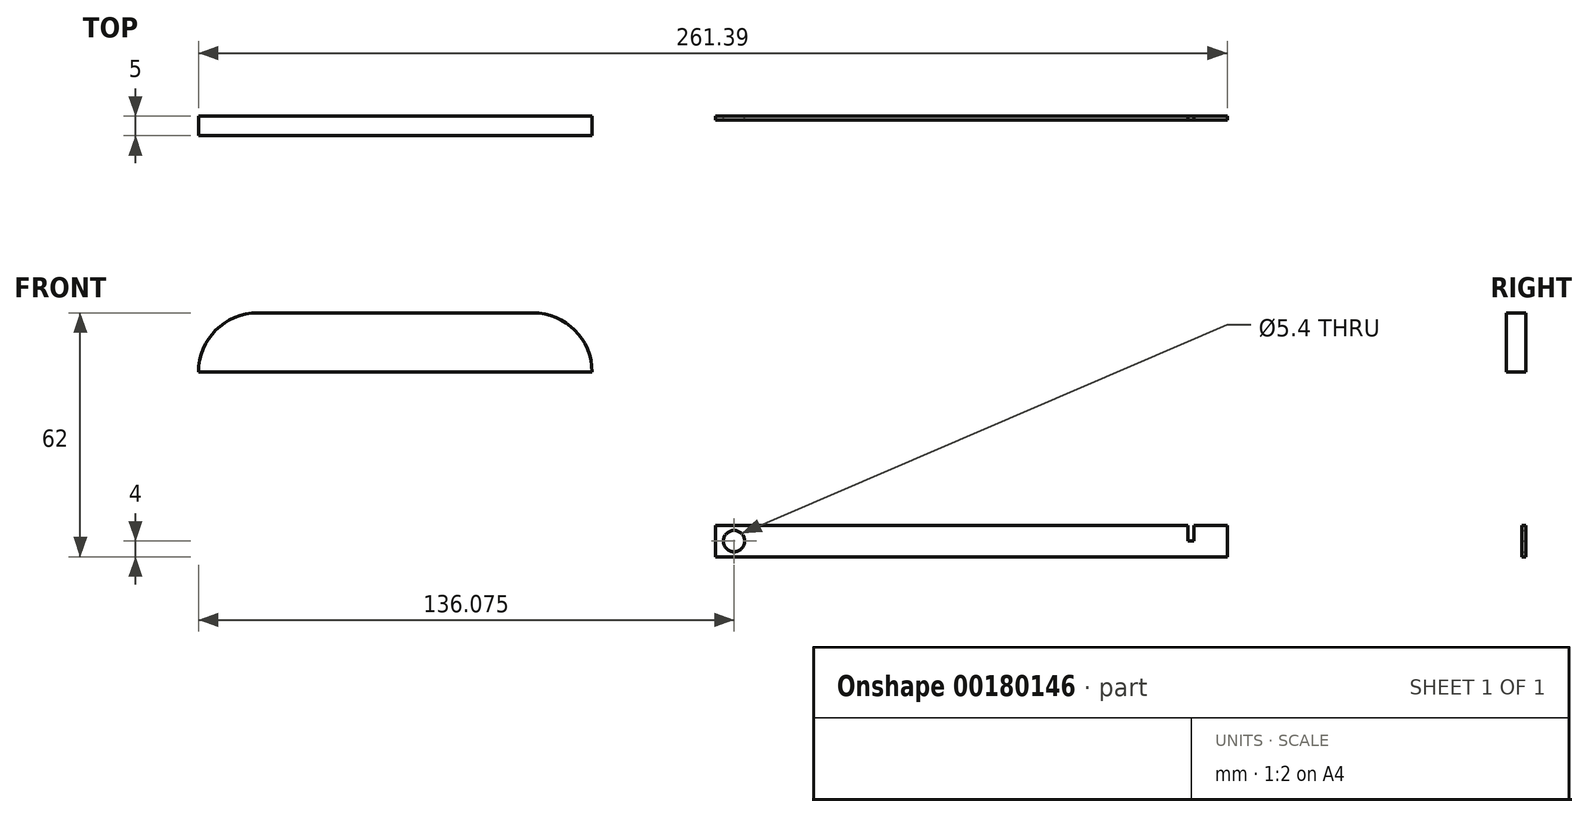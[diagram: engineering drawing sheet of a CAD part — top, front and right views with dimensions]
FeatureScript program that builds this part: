
annotation { "Feature Type Name" : "Feature", "Feature Type Description" : "" }
export const myFeature = defineFeature(function(context is Context, id is Id, definition is map)
    precondition{}
    {
        {
            var Q0;
            Q0=qCreatedBy(makeId("Front.planeOp"),FACE);
            var sketch = newSketch(context, id + "F0", { "sketchPlane" : qUnion([Q0])});
            skLineSegment(sketch, "E0", {"start": v(-91.47, 19.29) * mm, "end": v(8.53, 19.29) * mm});
            skLineSegment(sketch, "E1", {"start": v(8.53, 19.29) * mm, "end": v(8.53, 19.29) * mm});
            skLineSegment(sketch, "E2", {"start": v(-6.47, 34.29) * mm, "end": v(-76.47, 34.29) * mm});
            skLineSegment(sketch, "E3", {"start": v(-91.47, 19.29) * mm, "end": v(-91.47, 19.29) * mm});
            skPoint(sketch, "E4.visualSharp", {"position": v(-91.47, 34.29) * mm});
            skArc(sketch, "E4.filletArc", {"start": v(-76.47, 34.29) * mm, "mid": v(-87.08, 29.9) * mm, "end": v(-91.47, 19.29) * mm});
            skPoint(sketch, "E5.visualSharp", {"position": v(8.53, 34.29) * mm});
            skArc(sketch, "E5.filletArc", {"start": v(8.53, 19.29) * mm, "mid": v(4.14, 29.9) * mm, "end": v(-6.47, 34.29) * mm});
            skSolve(sketch);
        }
        {
            var Q0;
            Q0 = qSketchRegion(id + "F0", true);
            extrude(context, id + "F1", {"entities" : qUnion([Q0]), "depth" : 5 * mm});
        }
        {
            var Q0;
            Q0=qCreatedBy(makeId("Front.planeOp"),FACE);
            var sketch = newSketch(context, id + "F2", { "sketchPlane" : qUnion([Q0])});
            skLineSegment(sketch, "E6", {"start": v(39.92, -19.7) * mm, "end": v(39.92, -27.7) * mm});
            skLineSegment(sketch, "E7", {"start": v(39.92, -27.7) * mm, "end": v(169.92, -27.7) * mm});
            skLineSegment(sketch, "E8", {"start": v(169.92, -27.7) * mm, "end": v(169.92, -19.7) * mm});
            skLineSegment(sketch, "E9", {"start": v(169.92, -19.7) * mm, "end": v(39.92, -19.7) * mm});
            skLineSegment(sketch, "E10", {"start": v(159.92, -19.7) * mm, "end": v(159.92, -23.7) * mm});
            skPoint(sketch, "E10.endSnap0", {"position": v(169.92, -23.7) * mm});
            skLineSegment(sketch, "E11", {"start": v(159.92, -23.7) * mm, "end": v(161.42, -23.7) * mm});
            skLineSegment(sketch, "E12", {"start": v(161.42, -23.7) * mm, "end": v(161.42, -19.7) * mm});
            skCircle(sketch, "E13", {"center": v(44.6, -23.7) * mm, "radius": 2.7 * mm});
            skPoint(sketch, "E13.centerSnap0", {"position": v(39.92, -23.7) * mm});
            skSolve(sketch);
        }
        {
            var Q0;
            {var subQ3=sQuery(id+"F2.wireOp",EDGE,"E6");Q0=makeQuery(id+"F2.imprint","IMPRINT",FACE,{"disambiguationData":[TD([[makeQuery(id+"F2.imprint","IMPRINT",EDGE,{"derivedFrom":subQ3}),1.0]])]});}
            extrude(context, id + "F3", {"entities" : qUnion([Q0]), "depth" : 1 * mm});
        }
    });
